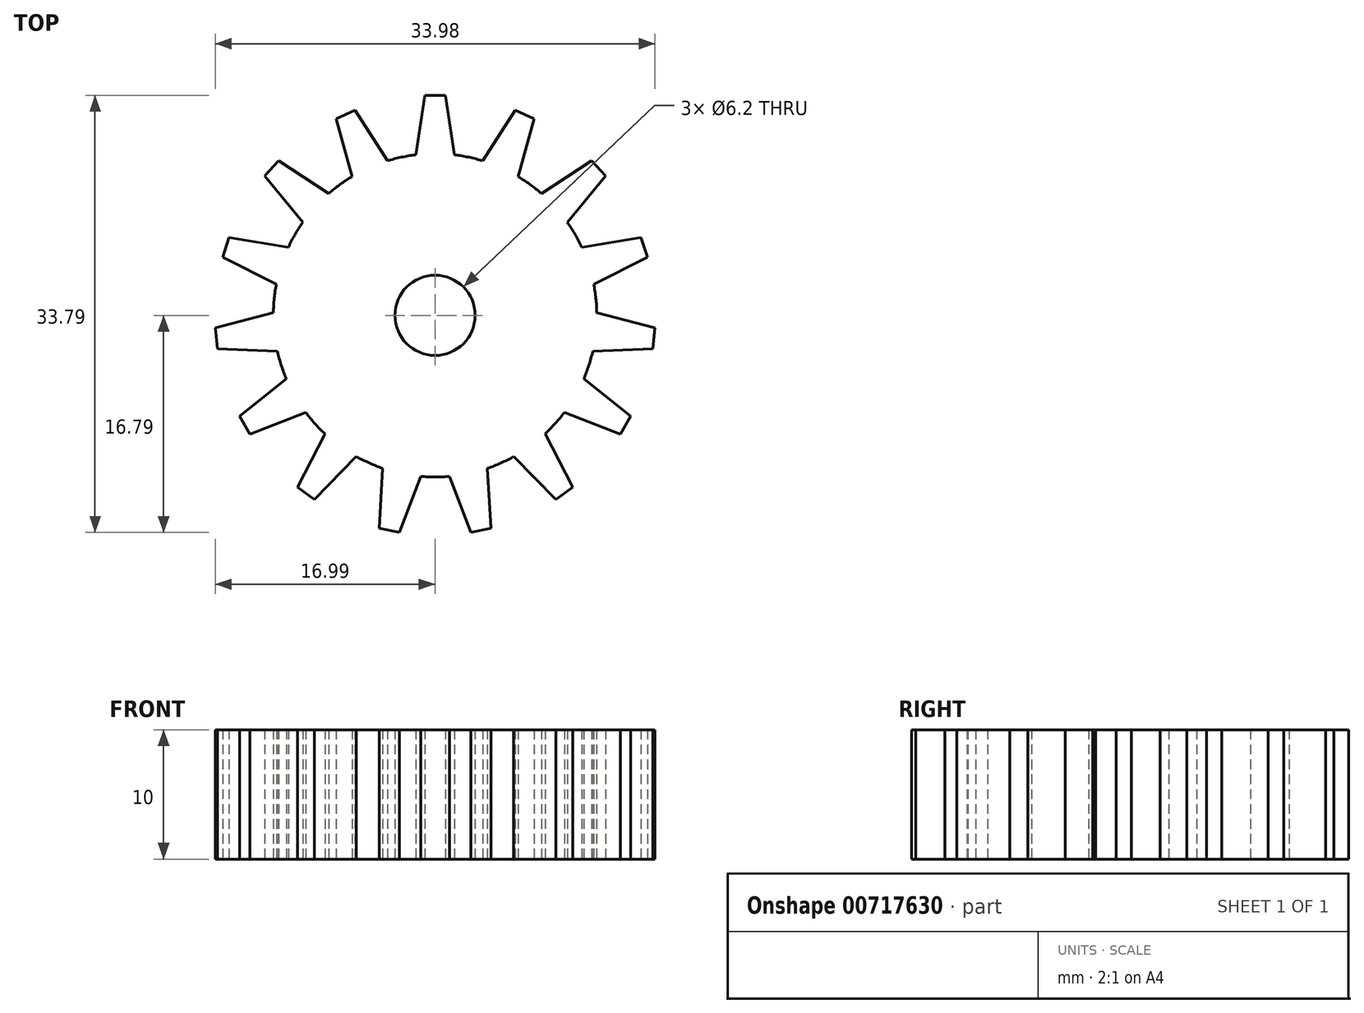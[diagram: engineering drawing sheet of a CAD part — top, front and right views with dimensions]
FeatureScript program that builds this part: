
annotation { "Feature Type Name" : "Feature", "Feature Type Description" : "" }
export const myFeature = defineFeature(function(context is Context, id is Id, definition is map)
    precondition{}
    {
        {
            var Q0;
            Q0=qCreatedBy(makeId("Top.planeOp"),FACE);
            var sketch = newSketch(context, id + "F0", { "sketchPlane" : qUnion([Q0])});
            skCircle(sketch, "E0", {"center": v(0, 0) * mm, "radius": 3.1 * mm});
            skCircle(sketch, "E1", {"center": v(0, 0) * mm, "radius": 12.5 * mm});
            skLineSegment(sketch, "E2", {"start": v(-1.5, 12.4) * mm, "end": v(1.5, 12.4) * mm});
            skLineSegment(sketch, "E3", {"start": v(-1.5, 12.4) * mm, "end": v(-0.8, 17) * mm});
            skLineSegment(sketch, "E4", {"start": v(-0.8, 17) * mm, "end": v(0.8, 17) * mm});
            skLineSegment(sketch, "E5", {"start": v(0.8, 17) * mm, "end": v(1.5, 12.4) * mm});
            skLineSegment(sketch, "E6.1.0", {"start": v(-6.18, 15.86) * mm, "end": v(-3.68, 11.95) * mm});
            skLineSegment(sketch, "E6.1.1", {"start": v(-7.65, 15.2) * mm, "end": v(-6.18, 15.86) * mm});
            skLineSegment(sketch, "E6.1.2", {"start": v(-6.42, 10.73) * mm, "end": v(-7.65, 15.2) * mm});
            skLineSegment(sketch, "E6.2.0", {"start": v(-12.1, 11.97) * mm, "end": v(-8.22, 9.42) * mm});
            skLineSegment(sketch, "E6.2.1", {"start": v(-13.17, 10.78) * mm, "end": v(-12.1, 11.97) * mm});
            skLineSegment(sketch, "E6.2.2", {"start": v(-10.23, 7.19) * mm, "end": v(-13.17, 10.78) * mm});
            skLineSegment(sketch, "E6.3.0", {"start": v(-15.92, 6.01) * mm, "end": v(-11.34, 5.26) * mm});
            skLineSegment(sketch, "E6.3.1", {"start": v(-16.42, 4.5) * mm, "end": v(-15.92, 6.01) * mm});
            skLineSegment(sketch, "E6.3.2", {"start": v(-12.27, 2.4) * mm, "end": v(-16.42, 4.5) * mm});
            skLineSegment(sketch, "E6.4.0", {"start": v(-17, -0.98) * mm, "end": v(-12.5, 0.2) * mm});
            skLineSegment(sketch, "E6.4.1", {"start": v(-16.82, -2.57) * mm, "end": v(-17, -0.98) * mm});
            skLineSegment(sketch, "E6.4.2", {"start": v(-12.18, -2.79) * mm, "end": v(-16.82, -2.57) * mm});
            skLineSegment(sketch, "E6.5.0", {"start": v(-15.12, -7.8) * mm, "end": v(-11.5, -4.9) * mm});
            skLineSegment(sketch, "E6.5.1", {"start": v(-14.32, -9.2) * mm, "end": v(-15.12, -7.8) * mm});
            skLineSegment(sketch, "E6.5.2", {"start": v(-10, -7.5) * mm, "end": v(-14.32, -9.2) * mm});
            skLineSegment(sketch, "E6.6.0", {"start": v(-10.64, -13.28) * mm, "end": v(-8.5, -9.16) * mm});
            skLineSegment(sketch, "E6.6.1", {"start": v(-9.35, -14.22) * mm, "end": v(-10.64, -13.28) * mm});
            skLineSegment(sketch, "E6.6.2", {"start": v(-6.08, -10.92) * mm, "end": v(-9.35, -14.22) * mm});
            skLineSegment(sketch, "E6.7.0", {"start": v(-4.32, -16.46) * mm, "end": v(-4.05, -11.83) * mm});
            skLineSegment(sketch, "E6.7.1", {"start": v(-2.75, -16.8) * mm, "end": v(-4.32, -16.46) * mm});
            skLineSegment(sketch, "E6.7.2", {"start": v(-1.11, -12.45) * mm, "end": v(-2.75, -16.8) * mm});
            skLineSegment(sketch, "E6.8.0", {"start": v(2.75, -16.8) * mm, "end": v(1.11, -12.45) * mm});
            skLineSegment(sketch, "E6.8.1", {"start": v(4.32, -16.46) * mm, "end": v(2.75, -16.8) * mm});
            skLineSegment(sketch, "E6.8.2", {"start": v(4.05, -11.83) * mm, "end": v(4.32, -16.46) * mm});
            skLineSegment(sketch, "E6.9.0", {"start": v(9.35, -14.22) * mm, "end": v(6.08, -10.92) * mm});
            skLineSegment(sketch, "E6.9.1", {"start": v(10.64, -13.28) * mm, "end": v(9.35, -14.22) * mm});
            skLineSegment(sketch, "E6.9.2", {"start": v(8.5, -9.16) * mm, "end": v(10.64, -13.28) * mm});
            skLineSegment(sketch, "E6.10.0", {"start": v(14.32, -9.2) * mm, "end": v(10, -7.5) * mm});
            skLineSegment(sketch, "E6.10.1", {"start": v(15.12, -7.8) * mm, "end": v(14.32, -9.2) * mm});
            skLineSegment(sketch, "E6.10.2", {"start": v(11.5, -4.9) * mm, "end": v(15.12, -7.8) * mm});
            skLineSegment(sketch, "E6.11.0", {"start": v(16.82, -2.57) * mm, "end": v(12.18, -2.79) * mm});
            skLineSegment(sketch, "E6.11.1", {"start": v(17, -0.98) * mm, "end": v(16.82, -2.57) * mm});
            skLineSegment(sketch, "E6.11.2", {"start": v(12.5, 0.2) * mm, "end": v(17, -0.98) * mm});
            skLineSegment(sketch, "E6.12.0", {"start": v(16.42, 4.5) * mm, "end": v(12.27, 2.4) * mm});
            skLineSegment(sketch, "E6.12.1", {"start": v(15.92, 6.01) * mm, "end": v(16.42, 4.5) * mm});
            skLineSegment(sketch, "E6.12.2", {"start": v(11.34, 5.26) * mm, "end": v(15.92, 6.01) * mm});
            skLineSegment(sketch, "E6.13.0", {"start": v(13.17, 10.78) * mm, "end": v(10.23, 7.19) * mm});
            skLineSegment(sketch, "E6.13.1", {"start": v(12.1, 11.97) * mm, "end": v(13.17, 10.78) * mm});
            skLineSegment(sketch, "E6.13.2", {"start": v(8.22, 9.42) * mm, "end": v(12.1, 11.97) * mm});
            skLineSegment(sketch, "E6.14.0", {"start": v(7.65, 15.2) * mm, "end": v(6.42, 10.73) * mm});
            skLineSegment(sketch, "E6.14.1", {"start": v(6.18, 15.86) * mm, "end": v(7.65, 15.2) * mm});
            skLineSegment(sketch, "E6.14.2", {"start": v(3.68, 11.95) * mm, "end": v(6.18, 15.86) * mm});
            skSolve(sketch);
        }
        {
            var Q0;
            {var subQ0=sQuery(id+"F0.wireOp",EDGE,"E6.11.0");Q0=makeQuery(id+"F0.imprint","IMPRINT",FACE,{"disambiguationData":[TD([[makeQuery(id+"F0.imprint","IMPRINT",EDGE,{"derivedFrom":subQ0}),-1.0]])]});}
            var Q1;
            {var subQ0=sQuery(id+"F0.wireOp",EDGE,"E6.9.0");Q1=makeQuery(id+"F0.imprint","IMPRINT",FACE,{"disambiguationData":[TD([[makeQuery(id+"F0.imprint","IMPRINT",EDGE,{"derivedFrom":subQ0}),-1.0]])]});}
            var Q2;
            {var subQ0=sQuery(id+"F0.wireOp",EDGE,"E6.10.0");Q2=makeQuery(id+"F0.imprint","IMPRINT",FACE,{"disambiguationData":[TD([[makeQuery(id+"F0.imprint","IMPRINT",EDGE,{"derivedFrom":subQ0}),-1.0]])]});}
            var Q3;
            {var subQ0=sQuery(id+"F0.wireOp",EDGE,"E6.12.0");Q3=makeQuery(id+"F0.imprint","IMPRINT",FACE,{"disambiguationData":[TD([[makeQuery(id+"F0.imprint","IMPRINT",EDGE,{"derivedFrom":subQ0}),-1.0]])]});}
            var Q4;
            {var subQ0=sQuery(id+"F0.wireOp",EDGE,"E6.13.0");Q4=makeQuery(id+"F0.imprint","IMPRINT",FACE,{"disambiguationData":[TD([[makeQuery(id+"F0.imprint","IMPRINT",EDGE,{"derivedFrom":subQ0}),-1.0]])]});}
            var Q5;
            {var subQ0=sQuery(id+"F0.wireOp",EDGE,"E6.14.0");Q5=makeQuery(id+"F0.imprint","IMPRINT",FACE,{"disambiguationData":[TD([[makeQuery(id+"F0.imprint","IMPRINT",EDGE,{"derivedFrom":subQ0}),-1.0]])]});}
            var Q6;
            {var subQ0=sQuery(id+"F0.wireOp",EDGE,"E3");Q6=makeQuery(id+"F0.imprint","IMPRINT",FACE,{"disambiguationData":[TD([[makeQuery(id+"F0.imprint","IMPRINT",EDGE,{"derivedFrom":subQ0}),-1.0]])]});}
            var Q7;
            {var subQ0=sQuery(id+"F0.wireOp",EDGE,"E6.1.0");Q7=makeQuery(id+"F0.imprint","IMPRINT",FACE,{"disambiguationData":[TD([[makeQuery(id+"F0.imprint","IMPRINT",EDGE,{"derivedFrom":subQ0}),-1.0]])]});}
            var Q8;
            {var subQ0=sQuery(id+"F0.wireOp",EDGE,"E6.2.0");Q8=makeQuery(id+"F0.imprint","IMPRINT",FACE,{"disambiguationData":[TD([[makeQuery(id+"F0.imprint","IMPRINT",EDGE,{"derivedFrom":subQ0}),-1.0]])]});}
            var Q9;
            {var subQ0=sQuery(id+"F0.wireOp",EDGE,"E6.3.0");Q9=makeQuery(id+"F0.imprint","IMPRINT",FACE,{"disambiguationData":[TD([[makeQuery(id+"F0.imprint","IMPRINT",EDGE,{"derivedFrom":subQ0}),-1.0]])]});}
            var Q10;
            {var subQ0=sQuery(id+"F0.wireOp",EDGE,"E6.4.0");Q10=makeQuery(id+"F0.imprint","IMPRINT",FACE,{"disambiguationData":[TD([[makeQuery(id+"F0.imprint","IMPRINT",EDGE,{"derivedFrom":subQ0}),-1.0]])]});}
            var Q11;
            {var subQ0=sQuery(id+"F0.wireOp",EDGE,"E6.5.0");Q11=makeQuery(id+"F0.imprint","IMPRINT",FACE,{"disambiguationData":[TD([[makeQuery(id+"F0.imprint","IMPRINT",EDGE,{"derivedFrom":subQ0}),-1.0]])]});}
            var Q12;
            {var subQ0=sQuery(id+"F0.wireOp",EDGE,"E6.6.0");Q12=makeQuery(id+"F0.imprint","IMPRINT",FACE,{"disambiguationData":[TD([[makeQuery(id+"F0.imprint","IMPRINT",EDGE,{"derivedFrom":subQ0}),-1.0]])]});}
            var Q13;
            {var subQ0=sQuery(id+"F0.wireOp",EDGE,"E6.7.0");Q13=makeQuery(id+"F0.imprint","IMPRINT",FACE,{"disambiguationData":[TD([[makeQuery(id+"F0.imprint","IMPRINT",EDGE,{"derivedFrom":subQ0}),-1.0]])]});}
            var Q14;
            {var subQ0=sQuery(id+"F0.wireOp",EDGE,"E6.8.0");Q14=makeQuery(id+"F0.imprint","IMPRINT",FACE,{"disambiguationData":[TD([[makeQuery(id+"F0.imprint","IMPRINT",EDGE,{"derivedFrom":subQ0}),-1.0]])]});}
            var Q15;
            Q15=makeQuery(id+"F0.imprint","IMPRINT",FACE,{"disambiguationData":[TD([[makeQuery(id+"F0.imprint","IMPRINT",EDGE,{"derivedFrom":sQuery(id+"F0.wireOp",EDGE,"E0")}),-1.0]])]});
            var Q16;
            {var subQ0=sQuery(id+"F0.wireOp",EDGE,"E2");Q16=makeQuery(id+"F0.imprint","IMPRINT",FACE,{"disambiguationData":[TD([[makeQuery(id+"F0.imprint","IMPRINT",EDGE,{"derivedFrom":subQ0}),1.0]])]});}
            extrude(context, id + "F1", {"entities" : qUnion([Q0, Q1, Q2, Q3, Q4, Q5, Q6, Q7, Q8, Q9, Q10, Q11, Q12, Q13, Q14, Q15, Q16]), "depth" : 10 * mm, "offsetDistance" : 25 * mm});
        }
    });
